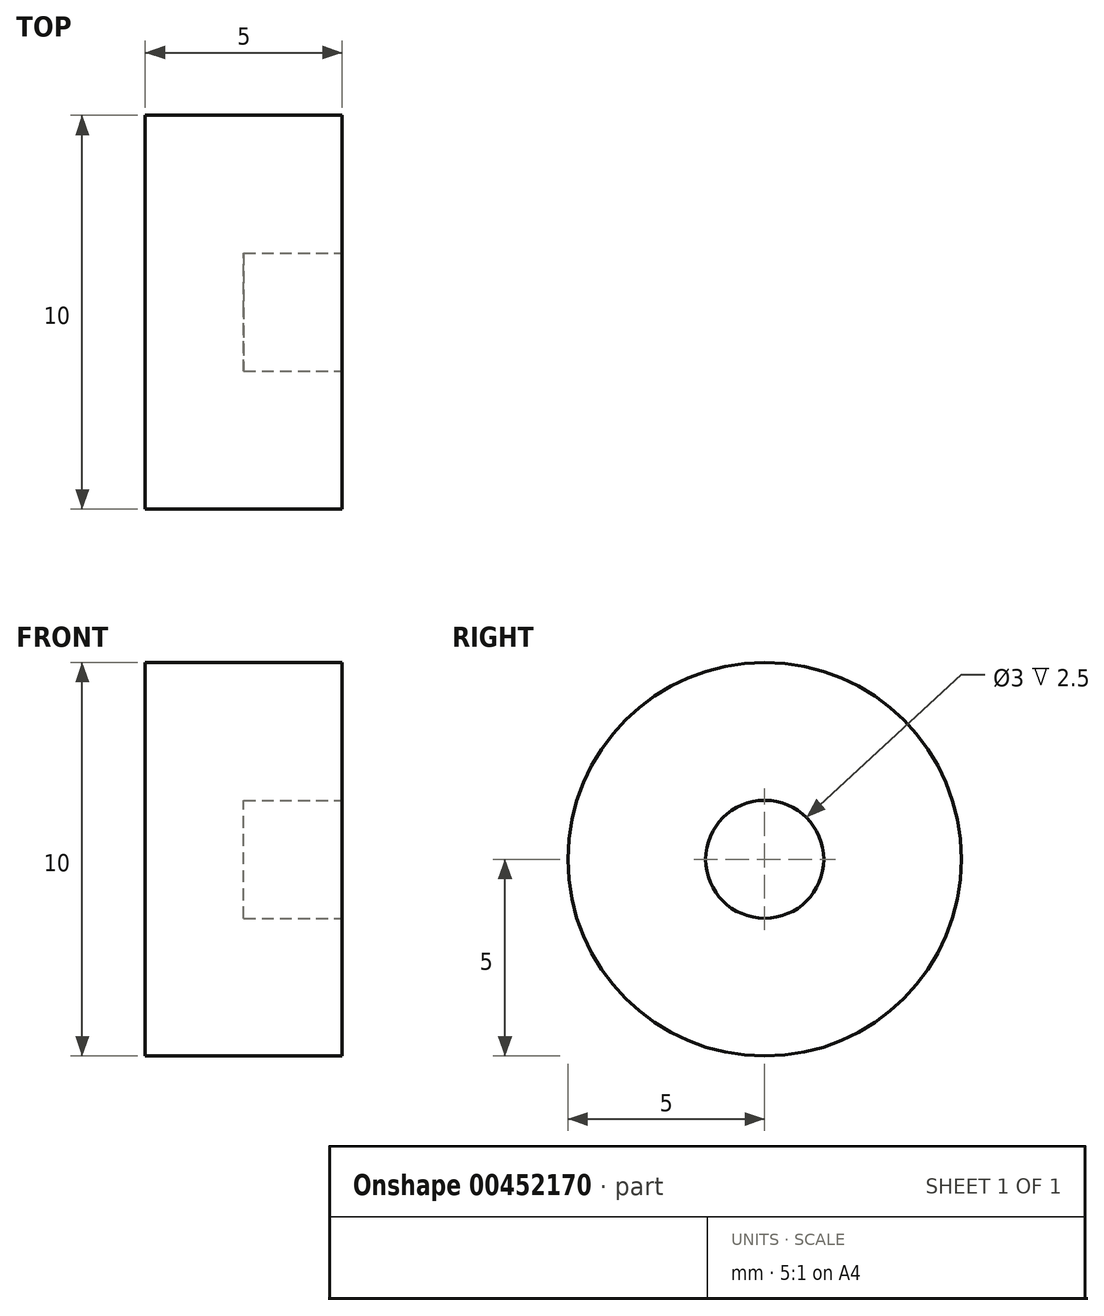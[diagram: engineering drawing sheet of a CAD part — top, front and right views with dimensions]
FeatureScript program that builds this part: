
annotation { "Feature Type Name" : "Feature", "Feature Type Description" : "" }
export const myFeature = defineFeature(function(context is Context, id is Id, definition is map)
    precondition{}
    {
        {
            var Q0;
            Q0=qCreatedBy(makeId("Right.planeOp"),FACE);
            var sketch = newSketch(context, id + "F0", { "sketchPlane" : qUnion([Q0])});
            skCircle(sketch, "E0", {"center": v(0, 0) * mm, "radius": 5 * mm});
            skSolve(sketch);
        }
        {
            var Q0;
            Q0=makeQuery(id+"F0.imprint","IMPRINT",FACE,{"disambiguationData":[TD([[makeQuery(id+"F0.imprint","IMPRINT",EDGE,{"derivedFrom":sQuery(id+"F0.wireOp",EDGE,"E0")}),1.0]])]});
            extrude(context, id + "F1", {"entities" : qUnion([Q0]), "depth" : 5 * mm});
        }
        {
            var Q0;
            Q0=makeQuery(id+"F1.opExtrude","CAP_FACE",FACE,{"disambiguationData":[OSD([sQuery(id+"F0.wireOp",EDGE,"E0")])],"isStart":false});
            var sketch = newSketch(context, id + "F2", { "sketchPlane" : qUnion([Q0])});
            skCircle(sketch, "E1", {"center": v(0, 0) * mm, "radius": 1.5 * mm});
            skSolve(sketch);
        }
        {
            var Q0;
            Q0 = qSketchRegion(id + "F2", true);
            extrude(context, id + "F3", {"entities" : qUnion([Q0]), "operationType" : NewBodyOperationType.REMOVE, "oppositeDirection" : true, "depth" : 2.5 * mm});
        }
    });
